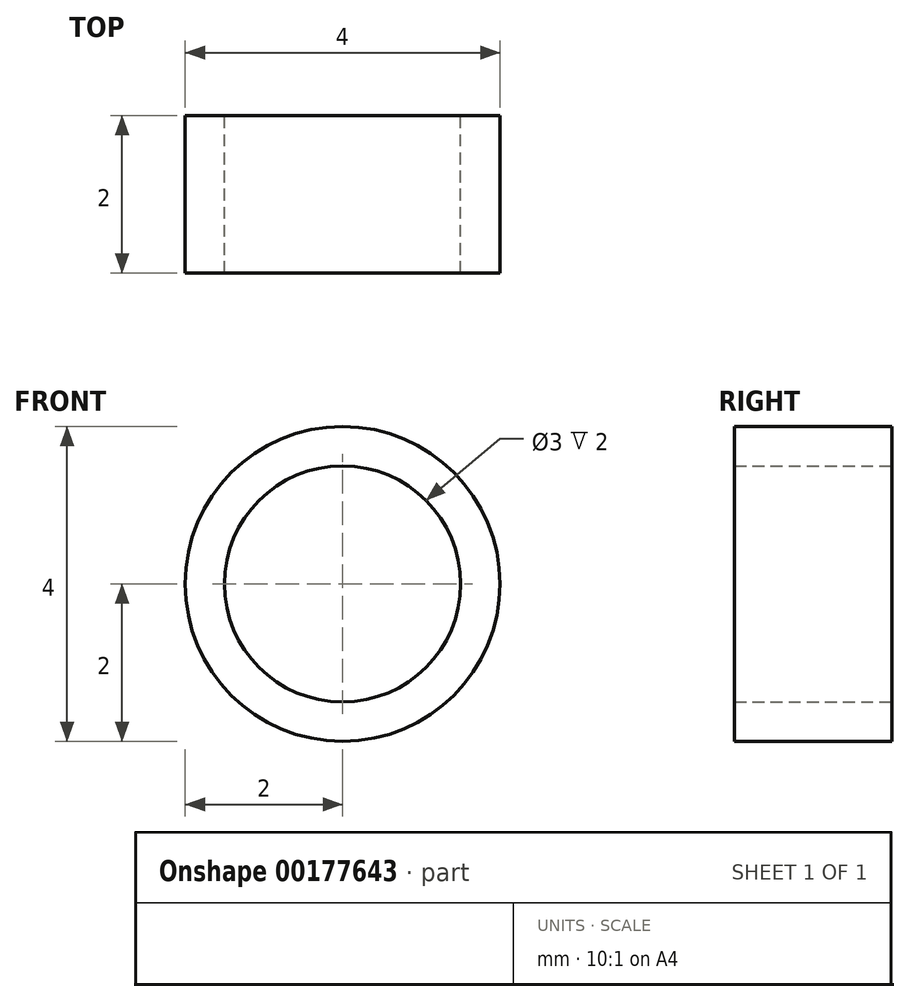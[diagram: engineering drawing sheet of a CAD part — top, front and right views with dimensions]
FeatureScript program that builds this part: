
annotation { "Feature Type Name" : "Feature", "Feature Type Description" : "" }
export const myFeature = defineFeature(function(context is Context, id is Id, definition is map)
    precondition{}
    {
        {
            var Q0;
            Q0=qCreatedBy(makeId("Front.planeOp"),FACE);
            var sketch = newSketch(context, id + "F0", { "sketchPlane" : qUnion([Q0])});
            skCircle(sketch, "E0", {"center": v(0, 0) * mm, "radius": 2 * mm});
            skCircle(sketch, "E1", {"center": v(0, 0) * mm, "radius": 1.5 * mm});
            skSolve(sketch);
        }
        {
            var Q0;
            Q0 = qSketchRegion(id + "F0", true);
            extrude(context, id + "F1", {"entities" : qUnion([Q0]), "depth" : 2 * mm});
        }
    });
